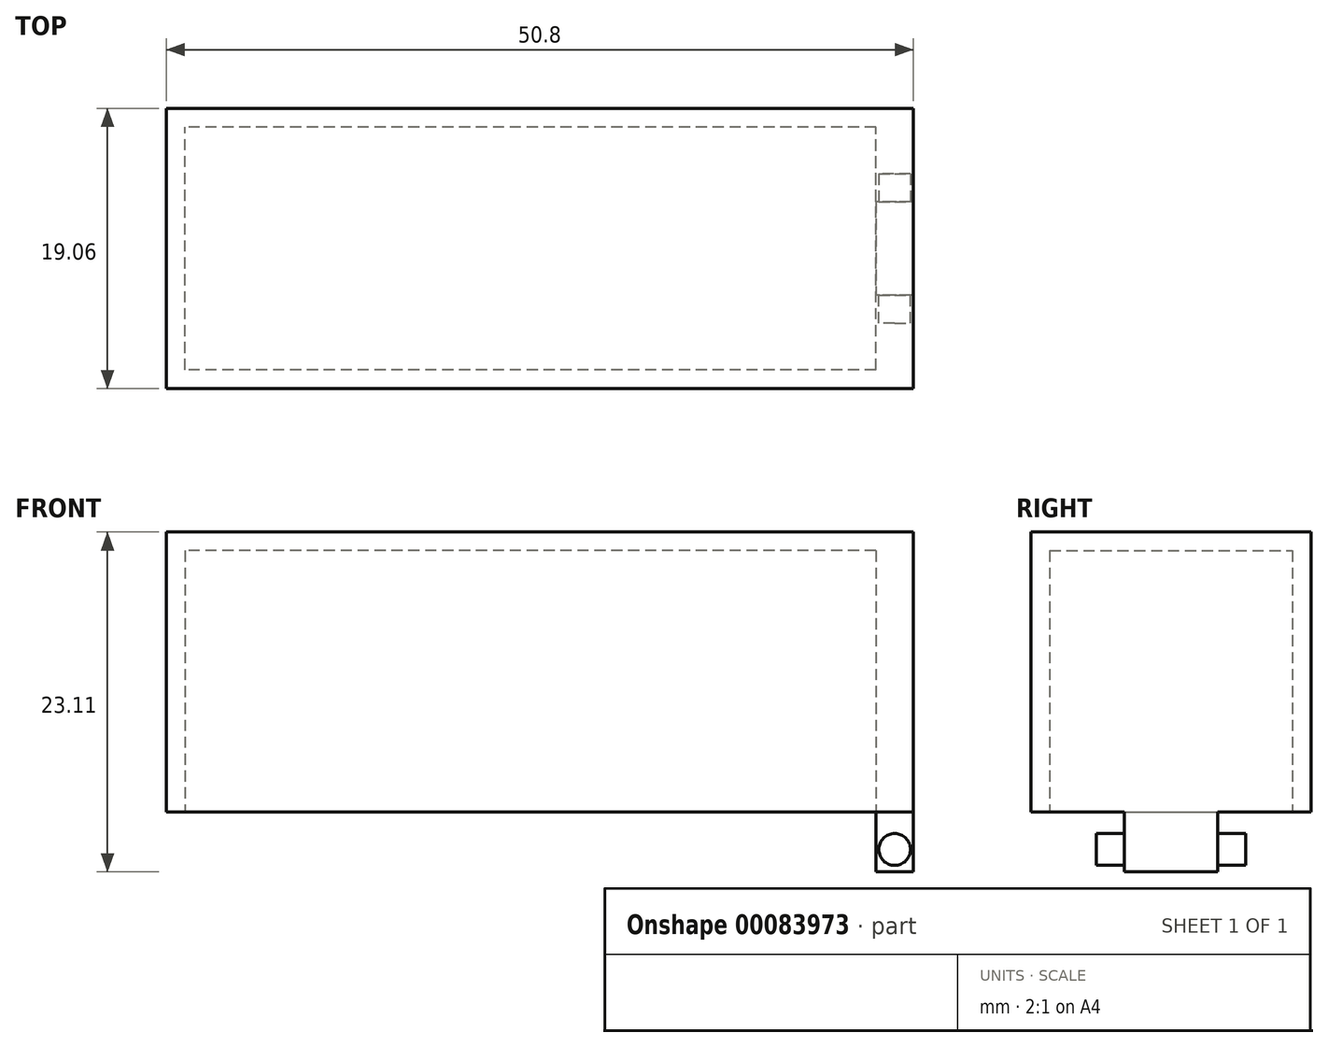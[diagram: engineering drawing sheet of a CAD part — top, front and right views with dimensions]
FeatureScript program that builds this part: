
annotation { "Feature Type Name" : "Feature", "Feature Type Description" : "" }
export const myFeature = defineFeature(function(context is Context, id is Id, definition is map)
    precondition{}
    {
        {
            var Q0;
            Q0=qCreatedBy(makeId("Top.planeOp"),FACE);
            var sketch = newSketch(context, id + "F0", { "sketchPlane" : qUnion([Q0])});
            skLineSegment(sketch, "E0.bottom", {"start": v(25.4, -9.52) * mm, "end": v(-25.4, -9.53) * mm});
            skLineSegment(sketch, "E0.top", {"start": v(25.4, 9.53) * mm, "end": v(-25.4, 9.52) * mm});
            skLineSegment(sketch, "E0.left", {"start": v(25.4, -9.52) * mm, "end": v(25.4, 9.53) * mm});
            skLineSegment(sketch, "E0.right", {"start": v(-25.4, -9.53) * mm, "end": v(-25.4, 9.52) * mm});
            skPoint(sketch, "E0.middle", {"position": v(0, 0) * mm});
            skSolve(sketch);
        }
        {
            var Q0;
            Q0 = qSketchRegion(id + "F0", true);
            extrude(context, id + "F1", {"entities" : qUnion([Q0]), "depth" : 19.05 * mm});
        }
        {
            var Q0;
            Q0=makeQuery(id+"F1.opExtrude","CAP_FACE",FACE,{"disambiguationData":[OSD([sQuery(id+"F0.wireOp",EDGE,"E0.bottom"),sQuery(id+"F0.wireOp",EDGE,"E0.top"),sQuery(id+"F0.wireOp",EDGE,"E0.left"),sQuery(id+"F0.wireOp",EDGE,"E0.right")])],"isStart":true});
            var sketch = newSketch(context, id + "F2", { "sketchPlane" : qUnion([Q0])});
            skLineSegment(sketch, "E1.bottom", {"start": v(25.4, -3.18) * mm, "end": v(22.86, -3.18) * mm});
            skLineSegment(sketch, "E1.top", {"start": v(25.4, 3.17) * mm, "end": v(22.86, 3.17) * mm});
            skLineSegment(sketch, "E1.left", {"start": v(25.4, -3.18) * mm, "end": v(25.4, 3.17) * mm});
            skLineSegment(sketch, "E1.right", {"start": v(22.86, -3.18) * mm, "end": v(22.86, 3.17) * mm});
            skSolve(sketch);
        }
        {
            var Q0;
            Q0 = qSketchRegion(id + "F2", true);
            extrude(context, id + "F3", {"entities" : qUnion([Q0]), "operationType" : NewBodyOperationType.ADD, "depth" : 4.06 * mm});
        }
        {
            var Q0;
            Q0=makeQuery(id+"F3.opExtrude","SWEPT_FACE",FACE,{"disambiguationData":[OSD([sQuery(id+"F2.wireOp",EDGE,"E1.top")])]});
            var sketch = newSketch(context, id + "F4", { "sketchPlane" : qUnion([Q0])});
            skCircle(sketch, "E2", {"center": v(24.13, -2.54) * mm, "radius": 1.08 * mm});
            skSolve(sketch);
        }
        {
            var Q0;
            Q0 = qSketchRegion(id + "F4", true);
            extrude(context, id + "F5", {"entities" : qUnion([Q0]), "operationType" : NewBodyOperationType.ADD, "depth" : 1.9 * mm});
        }
        {
            var Q0;
            Q0=makeQuery(id+"F3.opExtrude","SWEPT_FACE",FACE,{"disambiguationData":[OSD([sQuery(id+"F2.wireOp",EDGE,"E1.bottom")])]});
            var sketch = newSketch(context, id + "F6", { "sketchPlane" : qUnion([Q0])});
            skCircle(sketch, "E3", {"center": v(-24.13, -2.54) * mm, "radius": 1.08 * mm});
            skSolve(sketch);
        }
        {
            var Q0;
            Q0 = qSketchRegion(id + "F6", true);
            extrude(context, id + "F7", {"entities" : qUnion([Q0]), "operationType" : NewBodyOperationType.ADD, "depth" : 1.9 * mm});
        }
        {
            var Q0;
            Q0=makeQuery(id+"F1.opExtrude","CAP_FACE",FACE,{"disambiguationData":[OSD([sQuery(id+"F0.wireOp",EDGE,"E0.bottom"),sQuery(id+"F0.wireOp",EDGE,"E0.top"),sQuery(id+"F0.wireOp",EDGE,"E0.left"),sQuery(id+"F0.wireOp",EDGE,"E0.right")])],"isStart":true});
            shell(context, id + "F8", {"entities" : qUnion([Q0]), "thickness" : 1.27 * mm});
        }
        {
            var Q0;
            Q0=makeQuery(id+"F8.opShell","OFFSET_FACE",FACE,{"disambiguationData":[OSD([sQuery(id+"F0.wireOp",EDGE,"E0.left"),sQuery(id+"F2.wireOp",EDGE,"E1.left")])]});
            extrude(context, id + "F9", {"entities" : qUnion([Q0]), "operationType" : NewBodyOperationType.ADD, "depth" : 1.27 * mm});
        }
    });
